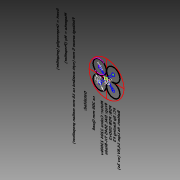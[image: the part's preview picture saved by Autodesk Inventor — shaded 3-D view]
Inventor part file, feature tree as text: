
AUTODESK INVENTOR PART (.ipt)
format: ipt  version: 2015 (Build 190159000, 159)  size: 92,160 bytes
history: native  units: mm
features: sketch x1
ambient origin geometry x8: Origin, YZ Plane, XZ Plane, XY Plane, X Axis, Y Axis, Z Axis, Center Point
feature tree (1):
  sketch  "Sketch1"  dims[d0=36.0mm d1=36.0mm d16=30.0mm d18=127.0mm d41=3.0mm d43=3.0mm d48=5.0mm]
